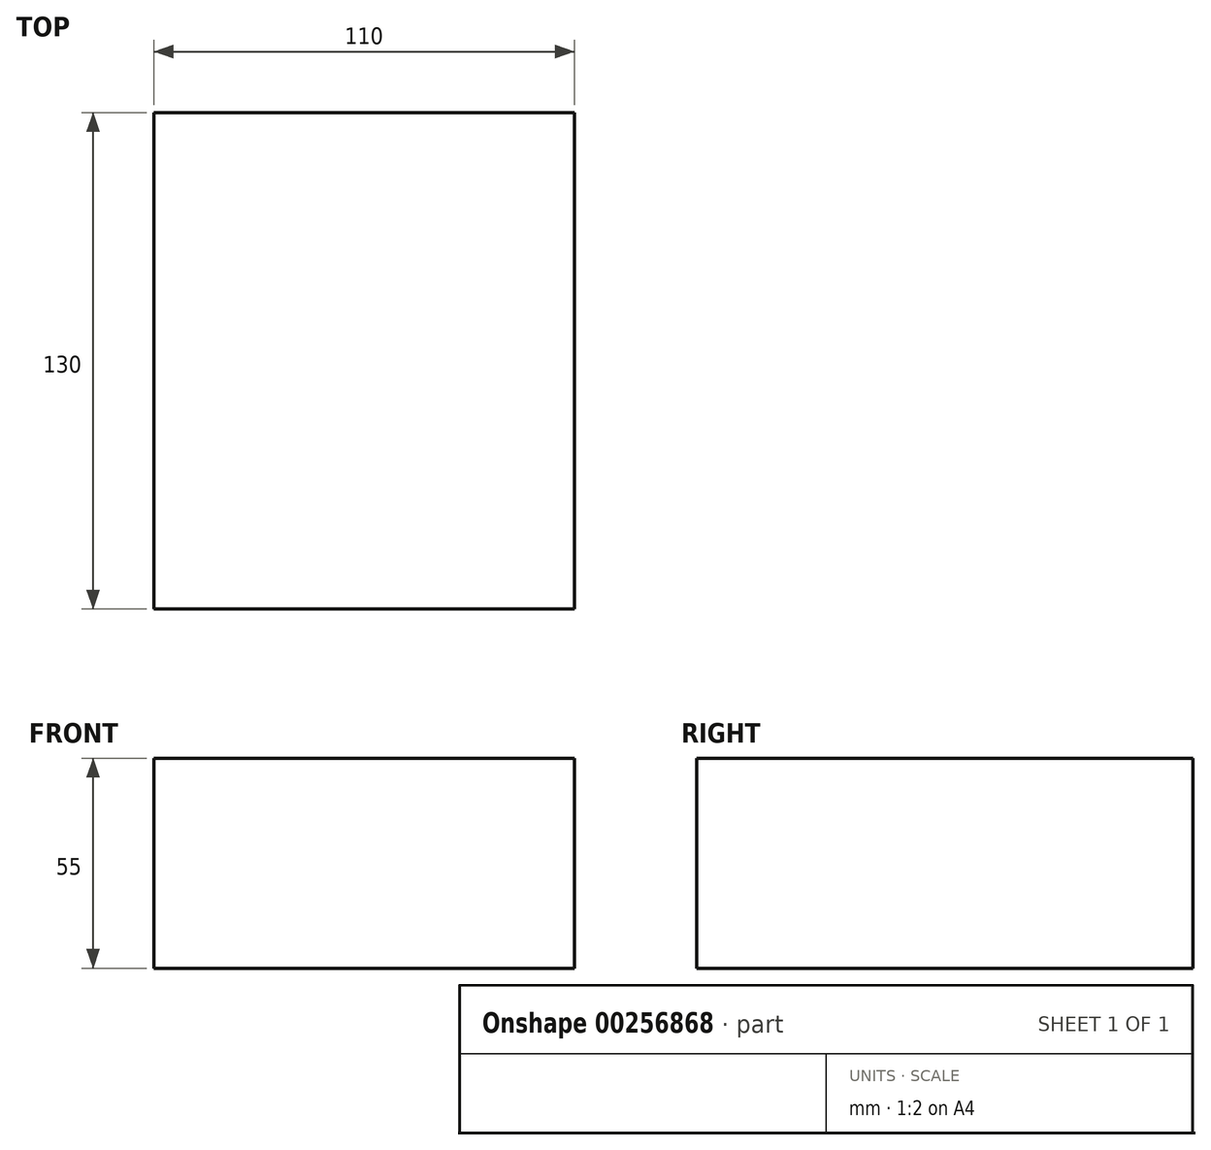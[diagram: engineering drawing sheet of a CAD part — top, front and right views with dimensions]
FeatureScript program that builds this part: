
annotation { "Feature Type Name" : "Feature", "Feature Type Description" : "" }
export const myFeature = defineFeature(function(context is Context, id is Id, definition is map)
    precondition{}
    {
        {
            var Q0;
            Q0=qCreatedBy(makeId("Front.planeOp"),FACE);
            var sketch = newSketch(context, id + "F0", { "sketchPlane" : qUnion([Q0])});
            skLineSegment(sketch, "E0.bottom", {"start": v(0, 0) * mm, "end": v(110, 0) * mm});
            skLineSegment(sketch, "E0.top", {"start": v(0, 55) * mm, "end": v(110, 55) * mm});
            skLineSegment(sketch, "E0.left", {"start": v(0, 0) * mm, "end": v(0, 55) * mm});
            skLineSegment(sketch, "E0.right", {"start": v(110, 0) * mm, "end": v(110, 55) * mm});
            skSolve(sketch);
        }
        {
            var Q0;
            Q0 = qSketchRegion(id + "F0", true);
            extrude(context, id + "F1", {"entities" : qUnion([Q0]), "depth" : 130 * mm});
        }
    });
